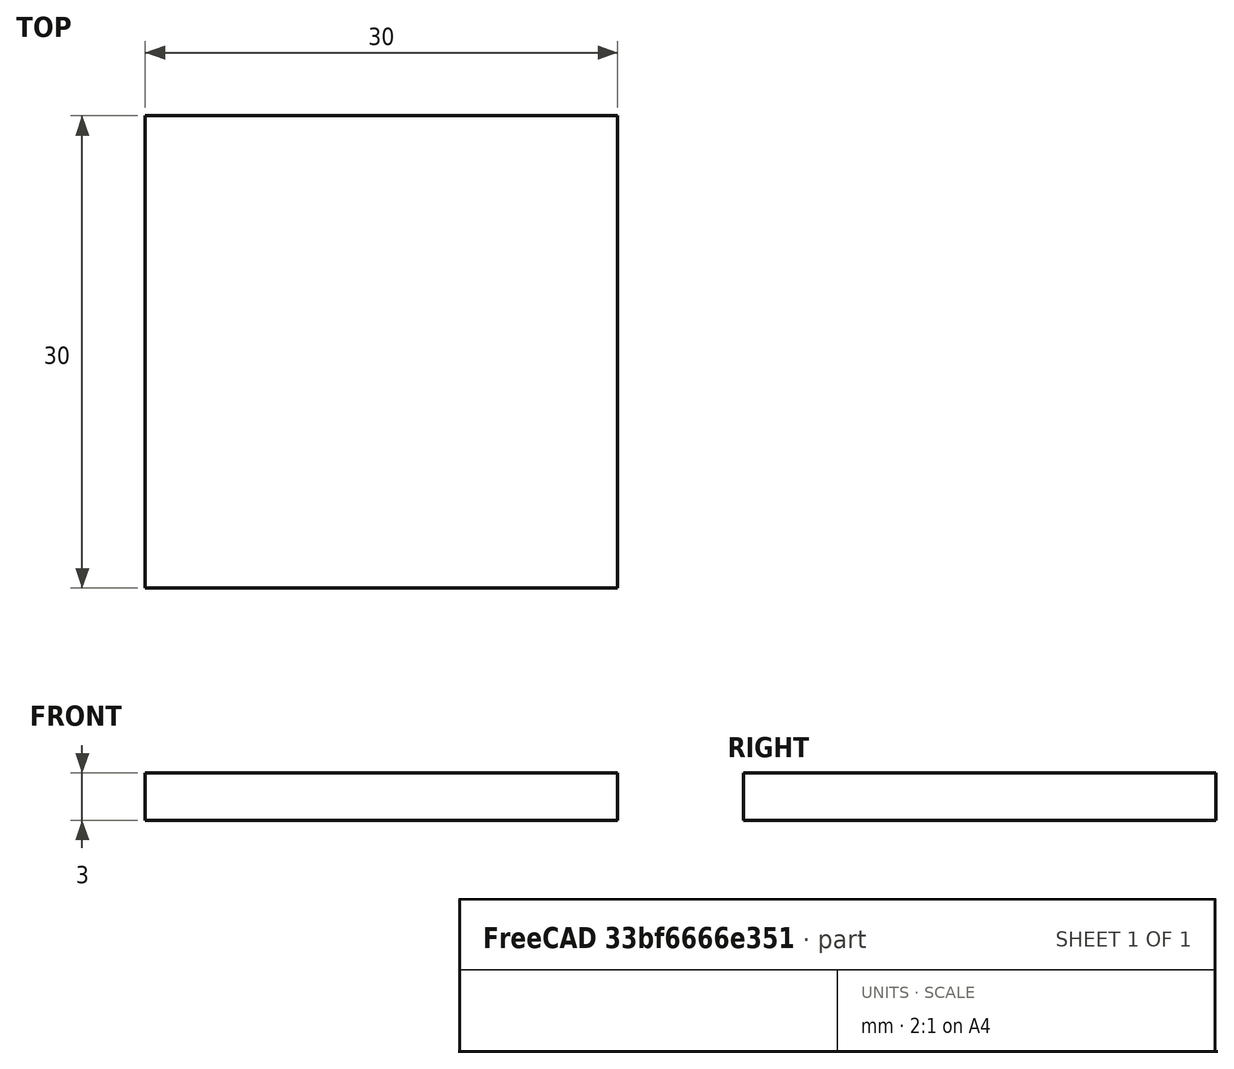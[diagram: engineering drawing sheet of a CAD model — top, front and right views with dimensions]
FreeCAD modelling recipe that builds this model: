
FCSTD DOCUMENT  (FreeCAD 0.19R)
Label: mirror_holder
License: All rights reserved
LicenseURL: http://en.wikipedia.org/wiki/All_rights_reserved
objects: Sketcher::SketchObject×1, PartDesign::Pad×1, PartDesign::Body×1
note: 4 computed .brp shape members not serialized (recipe doc carries the construction recipe); baked Part::Feature solids carry a one-line shape summary decoded from their .brp

FEATURE [Sketcher::SketchObject] Sketch
  FullyConstrained = true
  MapMode = 5
  Support = -> [XY_Plane]
  sketch-geometry (4):
    g0: LineSegment StartX=-15 StartY=15 StartZ=0 EndX=15 EndY=15 EndZ=0
    g1: LineSegment StartX=15 StartY=15 StartZ=0 EndX=15 EndY=-15 EndZ=0
    g2: LineSegment StartX=15 StartY=-15 StartZ=0 EndX=-15 EndY=-15 EndZ=0
    g3: LineSegment StartX=-15 StartY=-15 StartZ=0 EndX=-15 EndY=15 EndZ=0
  constraints (10):
    c: Coincident(g0,g1)
    c: Coincident(g1,g2)
    c: Coincident(g2,g3)
    c: Coincident(g3,g0)
    c: Horizontal(g2)
    c: Vertical(g1)
    c: Symmetric(g0,g0,g-2)
    c: Symmetric(g0,g2,g-1)
    c: Equal(g0,g3)
    c: DistanceX(g0,g0) = 30
FEATURE [PartDesign::Pad] Pad
  Direction = (1,1,1)
  Length = 3
  Length2 = 100
  Profile = -> Sketch
  Type = 0
FEATURE [PartDesign::Body] Body
  Group = -> [Sketch,Pad]
  Origin = -> Origin
  Tip = -> Pad
